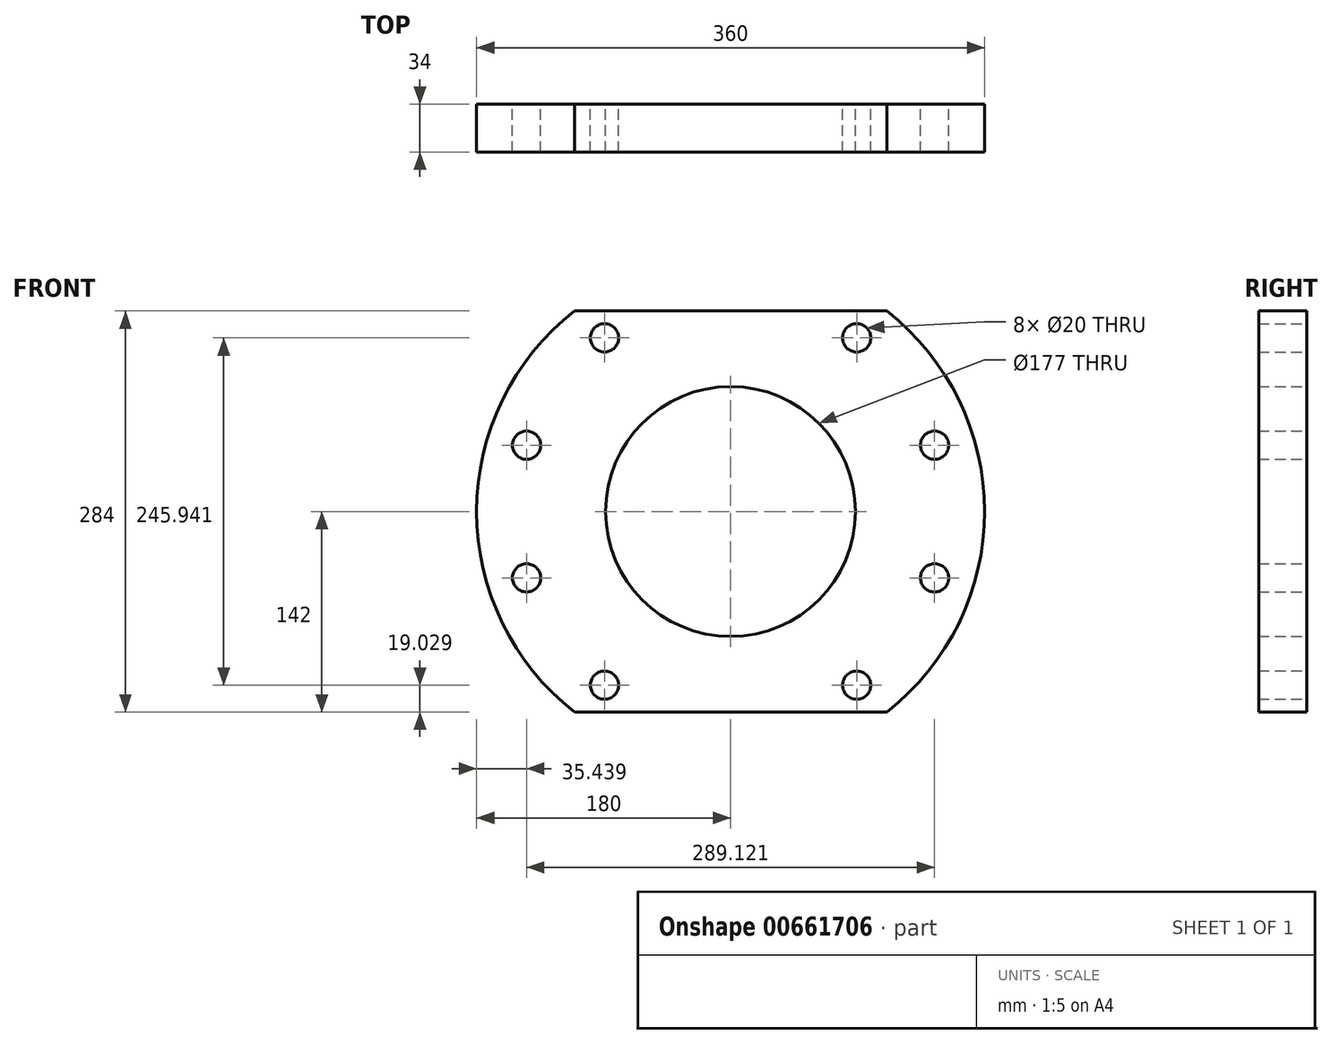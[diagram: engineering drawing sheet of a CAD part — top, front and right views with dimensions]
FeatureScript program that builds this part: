
annotation { "Feature Type Name" : "Feature", "Feature Type Description" : "" }
export const myFeature = defineFeature(function(context is Context, id is Id, definition is map)
    precondition{}
    {
        {
            var Q0;
            Q0=qCreatedBy(makeId("Front.planeOp"),FACE);
            var sketch = newSketch(context, id + "F0", { "sketchPlane" : qUnion([Q0])});
            skArc(sketch, "E0", {"start": v(-110.62, 142) * mm, "mid": v(-180, 0) * mm, "end": v(-110.62, -142) * mm});
            skCircle(sketch, "E1", {"center": v(0, 0) * mm, "radius": 88.5 * mm});
            skArc(sketch, "E2.trimOffspring", {"start": v(110.62, -142) * mm, "mid": v(180, 0) * mm, "end": v(110.62, 142) * mm});
            skCircle(sketch, "E3.1.0", {"center": v(-89.34, 122.97) * mm, "radius": 10 * mm});
            skCircle(sketch, "E3.2.0", {"center": v(-144.56, 46.97) * mm, "radius": 10 * mm});
            skCircle(sketch, "E3.3.0", {"center": v(-144.56, -46.97) * mm, "radius": 10 * mm});
            skCircle(sketch, "E3.4.0", {"center": v(-89.34, -122.97) * mm, "radius": 10 * mm});
            skCircle(sketch, "E3.6.0", {"center": v(89.34, -122.97) * mm, "radius": 10 * mm});
            skCircle(sketch, "E3.7.0", {"center": v(144.56, -46.97) * mm, "radius": 10 * mm});
            skCircle(sketch, "E3.8.0", {"center": v(144.56, 46.97) * mm, "radius": 10 * mm});
            skCircle(sketch, "E3.9.0", {"center": v(89.34, 122.97) * mm, "radius": 10 * mm});
            skLineSegment(sketch, "E4", {"start": v(0, 142) * mm, "end": v(110.62, 142) * mm});
            skLineSegment(sketch, "E5", {"start": v(110.62, 142) * mm, "end": v(-110.62, 142) * mm});
            skLineSegment(sketch, "E6", {"start": v(0, -142) * mm, "end": v(-110.62, -142) * mm});
            skLineSegment(sketch, "E7", {"start": v(-110.62, -142) * mm, "end": v(110.62, -142) * mm});
            skPoint(sketch, "E8.start.orphan", {"position": v(0, 160) * mm});
            skSolve(sketch);
        }
        {
            var Q0;
            Q0 = qSketchRegion(id + "F0", true);
            extrude(context, id + "F1", {"entities" : qUnion([Q0]), "depth" : 34 * mm, "offsetDistance" : 25 * mm});
        }
    });
